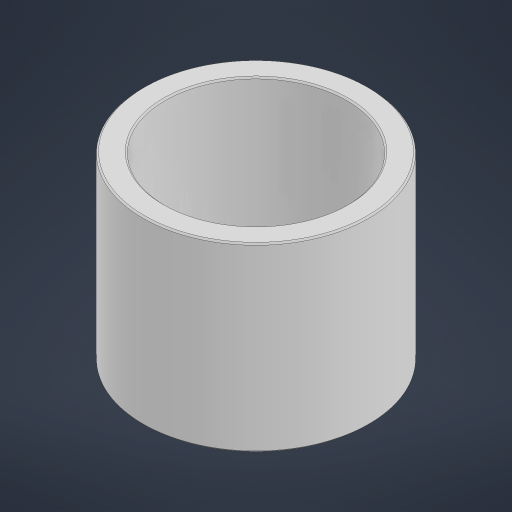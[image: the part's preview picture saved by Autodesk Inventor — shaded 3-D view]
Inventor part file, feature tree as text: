
AUTODESK INVENTOR PART (.ipt)
format: ipt  version: 2023 (Build 270158000, 158)  size: 170,496 bytes
history: native  units: in
note: dims shown in document units (in); Inventor stores cm internally (conversion verified against a paired STEP export)
features: chamfer x1
ambient origin geometry x8: Origin, YZ Plane, XZ Plane, XY Plane, X Axis, Y Axis, Z Axis, Center Point
bodies: Solid1 (feature_tree)
feature tree (1):
  chamfer  "Chamfer1"  [1 undecoded]
note: 1 required parameter value undecoded (feature->parameter linkage not recoverable at this tier; creation-order binding heuristic only, values carry confidence <= 0.55)
